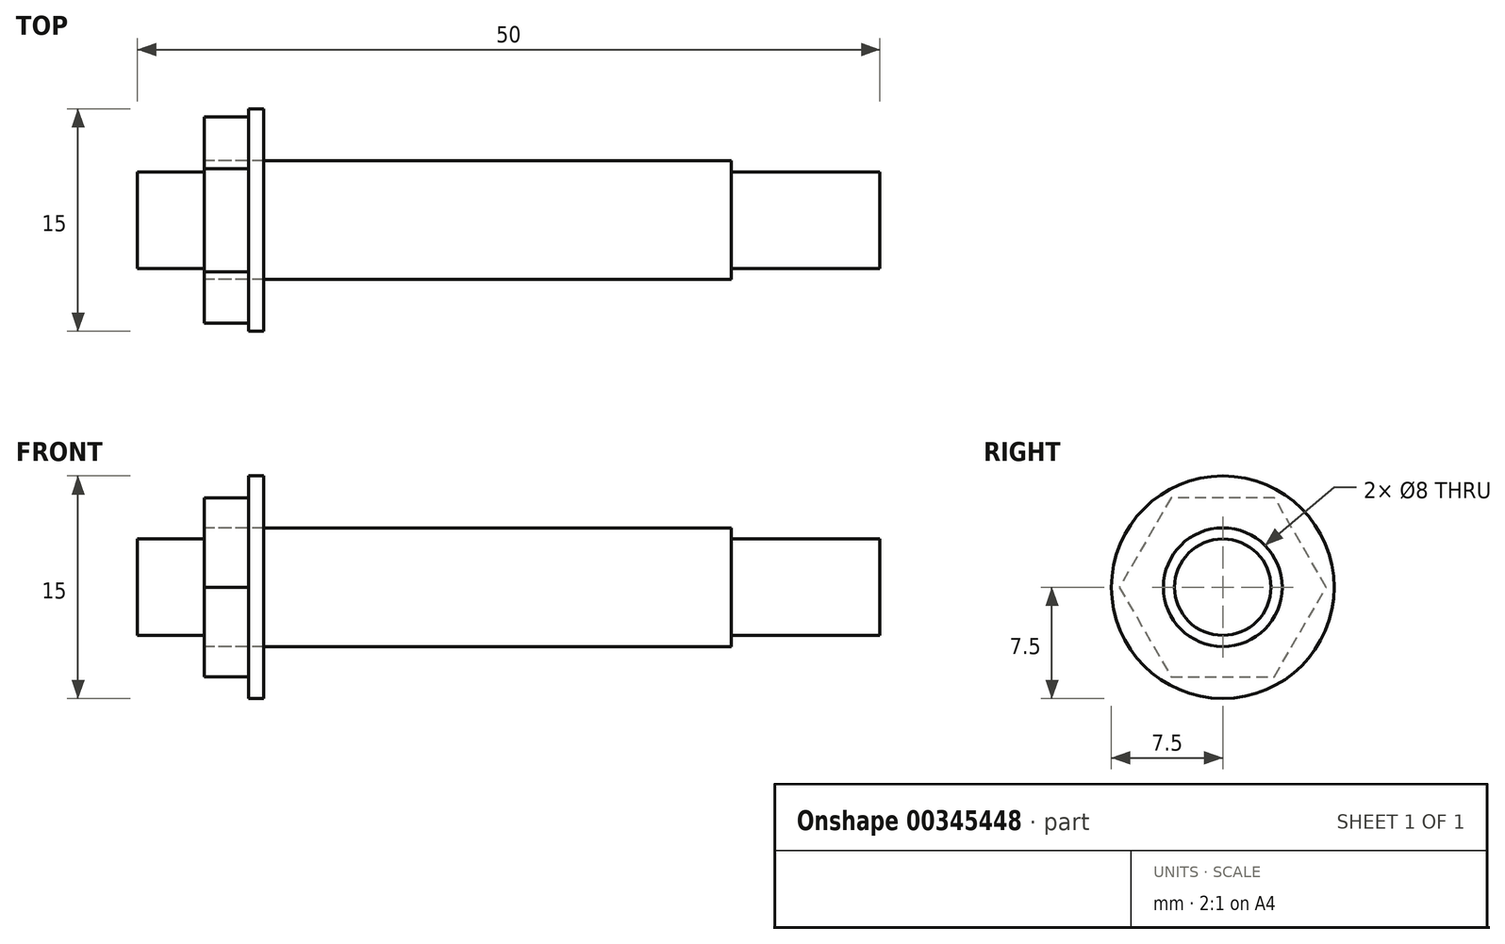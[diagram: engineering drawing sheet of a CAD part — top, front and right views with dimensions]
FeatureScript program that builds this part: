
annotation { "Feature Type Name" : "Feature", "Feature Type Description" : "" }
export const myFeature = defineFeature(function(context is Context, id is Id, definition is map)
    precondition{}
    {
        {
            var Q0;
            Q0=qCreatedBy(makeId("Front.planeOp"),FACE);
            var sketch = newSketch(context, id + "F0", { "sketchPlane" : qUnion([Q0])});
            skLineSegment(sketch, "E0", {"start": v(0, 0) * mm, "end": v(50, 0) * mm});
            skLineSegment(sketch, "E1", {"start": v(0, 0) * mm, "end": v(0, 3.25) * mm});
            skLineSegment(sketch, "E2", {"start": v(0, 3.25) * mm, "end": v(4.5, 3.25) * mm});
            skLineSegment(sketch, "E3", {"start": v(4.5, 3.25) * mm, "end": v(4.5, 4) * mm});
            skLineSegment(sketch, "E4", {"start": v(4.5, 4) * mm, "end": v(40, 4) * mm});
            skLineSegment(sketch, "E5", {"start": v(40, 4) * mm, "end": v(40, 3.25) * mm});
            skLineSegment(sketch, "E6", {"start": v(40, 3.25) * mm, "end": v(50, 3.25) * mm});
            skLineSegment(sketch, "E7", {"start": v(50, 3.25) * mm, "end": v(50, 0) * mm});
            skSolve(sketch);
        }
        {
            var Q0;
            Q0=makeQuery(id+"F0.imprint","IMPRINT",FACE,{"disambiguationData":[TD([[makeQuery(id+"F0.imprint","IMPRINT",EDGE,{"derivedFrom":sQuery(id+"F0.wireOp",EDGE,"E0")}),1.0]])]});
            var Q1;
            Q1=sQuery(id+"F0.wireOp",EDGE,"E0");
            revolve(context, id + "F1", {"entities" : qUnion([Q0]), "axis" : qUnion([Q1]), "revolveType" : RevolveType.FULL});
        }
        {
            var Q0;
            Q0=makeQuery(id+"F1.opRevolve","SWEPT_FACE",FACE,{"disambiguationData":[OSD([sQuery(id+"F0.wireOp",EDGE,"E3")])]});
            var sketch = newSketch(context, id + "F2", { "sketchPlane" : qUnion([Q0])});
            skCircle(sketch, "E8.0", {"center": v(0, 0) * mm, "radius": 4 * mm});
            skCircle(sketch, "E9.cCircle", {"center": v(0, 0) * mm, "radius": 6.03 * mm, "construction": true});
            skLineSegment(sketch, "E9.0", {"start": v(-3.48, 6.03) * mm, "end": v(3.48, 6.03) * mm});
            skLineSegment(sketch, "E9.1", {"start": v(3.48, 6.03) * mm, "end": v(6.96, 0) * mm});
            skLineSegment(sketch, "E9.2", {"start": v(6.96, 0) * mm, "end": v(3.48, -6.03) * mm});
            skLineSegment(sketch, "E9.3", {"start": v(3.48, -6.03) * mm, "end": v(-3.48, -6.03) * mm});
            skLineSegment(sketch, "E9.4", {"start": v(-3.48, -6.03) * mm, "end": v(-6.96, 0) * mm});
            skLineSegment(sketch, "E9.5", {"start": v(-6.96, 0) * mm, "end": v(-3.48, 6.03) * mm});
            skPoint(sketch, "E9.0.midPoint", {"position": v(0, 6.03) * mm});
            skSolve(sketch);
        }
        {
            var Q0;
            Q0 = qSketchRegion(id + "F2", true);
            extrude(context, id + "F3", {"entities" : qUnion([Q0]), "oppositeDirection" : true, "depth" : 3 * mm});
        }
        {
            var Q0;
            Q0=makeQuery(id+"F3.opExtrude","CAP_FACE",FACE,{"disambiguationData":[OSD([sQuery(id+"F2.wireOp",EDGE,"E8.0"),sQuery(id+"F2.wireOp",EDGE,"E9.0"),sQuery(id+"F2.wireOp",EDGE,"E9.1"),sQuery(id+"F2.wireOp",EDGE,"E9.2"),sQuery(id+"F2.wireOp",EDGE,"E9.3"),sQuery(id+"F2.wireOp",EDGE,"E9.4"),sQuery(id+"F2.wireOp",EDGE,"E9.5")])],"isStart":false});
            var sketch = newSketch(context, id + "F4", { "sketchPlane" : qUnion([Q0])});
            skCircle(sketch, "E10.0", {"center": v(0, 0) * mm, "radius": 4 * mm});
            skCircle(sketch, "E11", {"center": v(0, 0) * mm, "radius": 7.5 * mm});
            skSolve(sketch);
        }
        {
            var Q0;
            Q0 = qSketchRegion(id + "F4", true);
            extrude(context, id + "F5", {"entities" : qUnion([Q0]), "depth" : 1 * mm});
        }
    });
